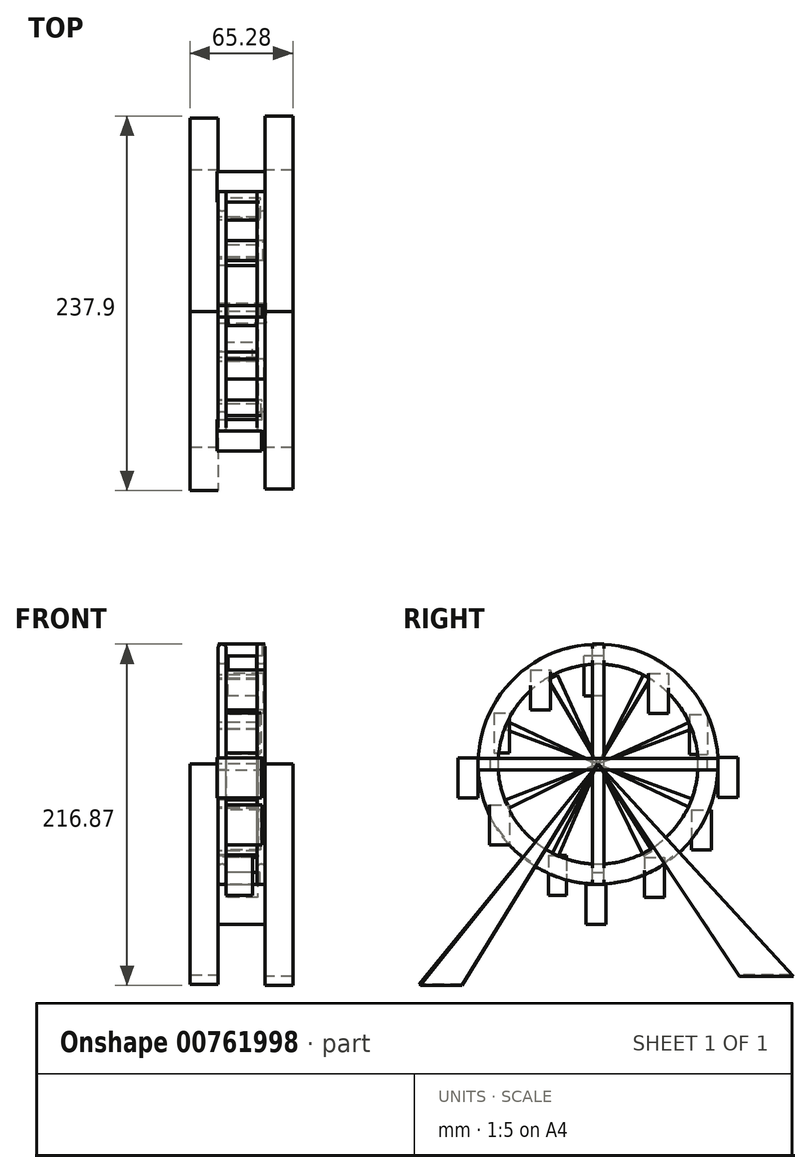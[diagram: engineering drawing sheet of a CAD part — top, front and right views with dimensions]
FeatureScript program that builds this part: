
annotation { "Feature Type Name" : "Feature", "Feature Type Description" : "" }
export const myFeature = defineFeature(function(context is Context, id is Id, definition is map)
    precondition{}
    {
        {
            var Q0;
            Q0=qCreatedBy(makeId("Right.planeOp"),FACE);
            var sketch = newSketch(context, id + "F0", { "sketchPlane" : qUnion([Q0])});
            skCircle(sketch, "E0", {"center": v(0, 0) * mm, "radius": 76.2 * mm});
            skSolve(sketch);
        }
        {
            var Q0;
            Q0 = qSketchRegion(id + "F0", true);
            extrude(context, id + "F1", {"entities" : qUnion([Q0]), "depth" : 5.08 * mm, "offsetDistance" : 25.4 * mm});
        }
        {
            var Q0;
            Q0=makeQuery(id+"F1.opExtrude","CAP_FACE",FACE,{"disambiguationData":[OSD([sQuery(id+"F0.wireOp",EDGE,"E0")])],"isStart":false});
            var sketch = newSketch(context, id + "F2", { "sketchPlane" : qUnion([Q0])});
            skCircle(sketch, "E1", {"center": v(0, 0) * mm, "radius": 63.5 * mm});
            skSolve(sketch);
        }
        {
            var Q0;
            Q0 = qSketchRegion(id + "F2", true);
            extrude(context, id + "F3", {"entities" : qUnion([Q0]), "operationType" : NewBodyOperationType.REMOVE, "endBound" : BoundingType.SYMMETRIC, "oppositeDirection" : true, "depth" : 56.9 * mm, "offsetDistance" : 25.4 * mm});
        }
        {
            var Q0;
            Q0=qCreatedBy(makeId("Right.planeOp"),FACE);
            var sketch = newSketch(context, id + "F4", { "sketchPlane" : qUnion([Q0])});
            skLineSegment(sketch, "E2.bottom", {"start": v(4.1, -63.24) * mm, "end": v(-4.1, -63.24) * mm});
            skLineSegment(sketch, "E2.top", {"start": v(4.1, 63.24) * mm, "end": v(-4.1, 63.24) * mm});
            skLineSegment(sketch, "E2.left", {"start": v(4.1, -63.24) * mm, "end": v(4.1, 63.24) * mm});
            skLineSegment(sketch, "E2.right", {"start": v(-4.1, -63.24) * mm, "end": v(-4.1, 63.24) * mm});
            skPoint(sketch, "E2.middle", {"position": v(0, 0) * mm});
            skSolve(sketch);
        }
        {
            var Q0;
            Q0=makeQuery(id+"F1.opExtrude","SWEPT_BODY",BODY,{"disambiguationData":[OSD([sQuery(id+"F0.wireOp",EDGE,"E0")])]});
            transform(context, id + "F5", {"entities" : qUnion([Q0]), "transformType" : TransformType.TRANSLATION_3D, "dx" : 9.4 * mm, "dy" : 0 * mm, "dz" : 0 * mm, "makeCopy" : true});
        }
        {
            var Q0;
            Q0=makeQuery(id+"F5.opPattern","COPY",BODY,{"derivedFrom":makeQuery(id+"F1.opExtrude","SWEPT_BODY",BODY,{"disambiguationData":[OSD([sQuery(id+"F0.wireOp",EDGE,"E0")])]}),"instanceName":"1"});
            transform(context, id + "F6", {"entities" : qUnion([Q0]), "transformType" : TransformType.TRANSLATION_3D, "dx" : 15.5 * mm, "dy" : 0 * mm, "dz" : 0 * mm, "makeCopy" : true});
        }
        {
            var Q0;
            Q0=makeQuery(id+"F5.opPattern","COPY",BODY,{"derivedFrom":makeQuery(id+"F1.opExtrude","SWEPT_BODY",BODY,{"disambiguationData":[OSD([sQuery(id+"F0.wireOp",EDGE,"E0")])]}),"instanceName":"1"});
            deleteBodies(context, id + "F7", {"entities" : qUnion([Q0])});
        }
        {
            var Q0;
            Q0=makeQuery(id+"F1.opExtrude","CAP_EDGE",EDGE,{"disambiguationData":[OSD([sQuery(id+"F0.wireOp",EDGE,"E0")])],"isStart":true});
            fillet(context, id + "F8", {"entities" : qUnion([Q0]), "radius" : 2.54 * mm, "tangentPropagation" : true, "allowEdgeOverflow" : false});
        }
        {
            var Q0;
            Q0=makeQuery(id+"F1.opExtrude","CAP_EDGE",EDGE,{"disambiguationData":[OSD([sQuery(id+"F0.wireOp",EDGE,"E0")])],"isStart":false});
            fillet(context, id + "F9", {"entities" : qUnion([Q0]), "radius" : 2.54 * mm, "tangentPropagation" : true, "allowEdgeOverflow" : false});
        }
        {
            var Q0;
            Q0=makeQuery(id+"F3.boolean.opBoolean","INTERSECT",EDGE,{"derivedFrom":[makeQuery(id+"F1.opExtrude","CAP_FACE",FACE,{"disambiguationData":[OSD([sQuery(id+"F0.wireOp",EDGE,"E0")])],"isStart":true}),makeQuery(id+"F3.opExtrude","SWEPT_FACE",FACE,{"disambiguationData":[OSD([sQuery(id+"F2.wireOp",EDGE,"E1")])]})]});
            fillet(context, id + "F10", {"entities" : qUnion([Q0]), "radius" : 2.54 * mm, "tangentPropagation" : true, "allowEdgeOverflow" : false});
        }
        {
            var Q0;
            Q0=makeQuery(id+"F3.boolean.opBoolean","INTERSECT",EDGE,{"derivedFrom":[makeQuery(id+"F1.opExtrude","CAP_FACE",FACE,{"disambiguationData":[OSD([sQuery(id+"F0.wireOp",EDGE,"E0")])],"isStart":false}),makeQuery(id+"F3.opExtrude","SWEPT_FACE",FACE,{"disambiguationData":[OSD([sQuery(id+"F2.wireOp",EDGE,"E1")])]})]});
            fillet(context, id + "F11", {"entities" : qUnion([Q0]), "radius" : 2.54 * mm, "tangentPropagation" : true, "allowEdgeOverflow" : false});
        }
        {
            var Q0;
            Q0=makeQuery(id+"F6.opPattern","COPY",EDGE,{"derivedFrom":makeQuery(id+"F5.opPattern","COPY",EDGE,{"derivedFrom":makeQuery(id+"F1.opExtrude","CAP_EDGE",EDGE,{"disambiguationData":[OSD([sQuery(id+"F0.wireOp",EDGE,"E0")])],"isStart":true}),"instanceName":"1"}),"instanceName":"1"});
            var Q1;
            Q1=makeQuery(id+"F6.opPattern","COPY",EDGE,{"derivedFrom":makeQuery(id+"F5.opPattern","COPY",EDGE,{"derivedFrom":makeQuery(id+"F3.boolean.opBoolean","INTERSECT",EDGE,{"derivedFrom":[makeQuery(id+"F1.opExtrude","CAP_FACE",FACE,{"disambiguationData":[OSD([sQuery(id+"F0.wireOp",EDGE,"E0")])],"isStart":true}),makeQuery(id+"F3.opExtrude","SWEPT_FACE",FACE,{"disambiguationData":[OSD([sQuery(id+"F2.wireOp",EDGE,"E1")])]})]}),"instanceName":"1"}),"instanceName":"1"});
            var Q2;
            Q2=makeQuery(id+"F6.opPattern","COPY",EDGE,{"derivedFrom":makeQuery(id+"F5.opPattern","COPY",EDGE,{"derivedFrom":makeQuery(id+"F3.boolean.opBoolean","INTERSECT",EDGE,{"derivedFrom":[makeQuery(id+"F1.opExtrude","CAP_FACE",FACE,{"disambiguationData":[OSD([sQuery(id+"F0.wireOp",EDGE,"E0")])],"isStart":false}),makeQuery(id+"F3.opExtrude","SWEPT_FACE",FACE,{"disambiguationData":[OSD([sQuery(id+"F2.wireOp",EDGE,"E1")])]})]}),"instanceName":"1"}),"instanceName":"1"});
            var Q3;
            Q3=makeQuery(id+"F6.opPattern","COPY",EDGE,{"derivedFrom":makeQuery(id+"F5.opPattern","COPY",EDGE,{"derivedFrom":makeQuery(id+"F1.opExtrude","CAP_EDGE",EDGE,{"disambiguationData":[OSD([sQuery(id+"F0.wireOp",EDGE,"E0")])],"isStart":false}),"instanceName":"1"}),"instanceName":"1"});
            fillet(context, id + "F12", {"entities" : qUnion([Q0, Q1, Q2, Q3]), "radius" : 2.54 * mm, "tangentPropagation" : true, "allowEdgeOverflow" : false});
        }
        {
            var Q0;
            Q0=qCreatedBy(makeId("Right.planeOp"),FACE);
            var sketch = newSketch(context, id + "F13", { "sketchPlane" : qUnion([Q0])});
            skLineSegment(sketch, "E3.bottom", {"start": v(3.62, -76.27) * mm, "end": v(-3.62, -76.27) * mm});
            skLineSegment(sketch, "E3.top", {"start": v(3.62, 76.27) * mm, "end": v(-3.62, 76.27) * mm});
            skLineSegment(sketch, "E3.left", {"start": v(3.62, -76.27) * mm, "end": v(3.62, 76.27) * mm});
            skLineSegment(sketch, "E3.right", {"start": v(-3.62, -76.27) * mm, "end": v(-3.62, 76.27) * mm});
            skPoint(sketch, "E3.middle", {"position": v(0, 0) * mm});
            skSolve(sketch);
        }
        {
            var Q0;
            Q0 = qSketchRegion(id + "F13", true);
            extrude(context, id + "F14", {"entities" : qUnion([Q0]), "depth" : 5.08 * mm, "offsetDistance" : 25.4 * mm});
        }
        {
            var Q0;
            Q0=makeQuery(id+"F14.opExtrude","SWEPT_BODY",BODY,{"disambiguationData":[OSD([sQuery(id+"F13.wireOp",EDGE,"E3.bottom"),sQuery(id+"F13.wireOp",EDGE,"E3.top"),sQuery(id+"F13.wireOp",EDGE,"E3.left"),sQuery(id+"F13.wireOp",EDGE,"E3.right")])]});
            transform(context, id + "F15", {"entities" : qUnion([Q0]), "transformType" : TransformType.TRANSLATION_3D, "dx" : 17.02 * mm, "dy" : 0 * mm, "dz" : 0 * mm, "makeCopy" : true});
        }
        {
            var Q0;
            Q0=makeQuery(id+"F15.opPattern","COPY",BODY,{"derivedFrom":makeQuery(id+"F14.opExtrude","SWEPT_BODY",BODY,{"disambiguationData":[OSD([sQuery(id+"F13.wireOp",EDGE,"E3.bottom"),sQuery(id+"F13.wireOp",EDGE,"E3.top"),sQuery(id+"F13.wireOp",EDGE,"E3.left"),sQuery(id+"F13.wireOp",EDGE,"E3.right")])]}),"instanceName":"1"});
            transform(context, id + "F16", {"entities" : qUnion([Q0]), "transformType" : TransformType.TRANSLATION_3D, "dx" : 7.62 * mm, "dy" : 0 * mm, "dz" : 0 * mm, "makeCopy" : true});
        }
        {
            var Q0;
            Q0=makeQuery(id+"F15.opPattern","COPY",BODY,{"derivedFrom":makeQuery(id+"F14.opExtrude","SWEPT_BODY",BODY,{"disambiguationData":[OSD([sQuery(id+"F13.wireOp",EDGE,"E3.bottom"),sQuery(id+"F13.wireOp",EDGE,"E3.top"),sQuery(id+"F13.wireOp",EDGE,"E3.left"),sQuery(id+"F13.wireOp",EDGE,"E3.right")])]}),"instanceName":"1"});
            deleteBodies(context, id + "F17", {"entities" : qUnion([Q0])});
        }
        {
            var Q0;
            Q0=makeQuery(id+"F14.opExtrude","CAP_FACE",FACE,{"disambiguationData":[OSD([sQuery(id+"F13.wireOp",EDGE,"E3.bottom"),sQuery(id+"F13.wireOp",EDGE,"E3.top"),sQuery(id+"F13.wireOp",EDGE,"E3.left"),sQuery(id+"F13.wireOp",EDGE,"E3.right")])],"isStart":false});
            var sketch = newSketch(context, id + "F18", { "sketchPlane" : qUnion([Q0])});
            skLineSegment(sketch, "E4.bottom", {"start": v(-3.62, 76.27) * mm, "end": v(3.62, 76.27) * mm});
            skLineSegment(sketch, "E4.top", {"start": v(-3.62, 68.65) * mm, "end": v(3.62, 68.65) * mm});
            skLineSegment(sketch, "E4.left", {"start": v(-3.62, 76.27) * mm, "end": v(-3.62, 68.65) * mm});
            skLineSegment(sketch, "E4.right", {"start": v(3.62, 76.27) * mm, "end": v(3.62, 68.65) * mm});
            skSolve(sketch);
        }
        {
            var Q0;
            Q0 = qSketchRegion(id + "F18", true);
            extrude(context, id + "F19", {"entities" : qUnion([Q0]), "depth" : 23.1 * mm, "offsetDistance" : 25.4 * mm});
        }
        {
            var Q0;
            Q0=makeQuery(id+"F14.opExtrude","CAP_FACE",FACE,{"disambiguationData":[OSD([sQuery(id+"F13.wireOp",EDGE,"E3.bottom"),sQuery(id+"F13.wireOp",EDGE,"E3.top"),sQuery(id+"F13.wireOp",EDGE,"E3.left"),sQuery(id+"F13.wireOp",EDGE,"E3.right")])],"isStart":false});
            var sketch = newSketch(context, id + "F20", { "sketchPlane" : qUnion([Q0])});
            skLineSegment(sketch, "E5.bottom", {"start": v(-3.62, -76.27) * mm, "end": v(3.62, -76.27) * mm});
            skLineSegment(sketch, "E5.top", {"start": v(-3.62, -68.65) * mm, "end": v(3.62, -68.65) * mm});
            skLineSegment(sketch, "E5.left", {"start": v(-3.62, -76.27) * mm, "end": v(-3.62, -68.65) * mm});
            skLineSegment(sketch, "E5.right", {"start": v(3.62, -76.27) * mm, "end": v(3.62, -68.65) * mm});
            skSolve(sketch);
        }
        {
            var Q0;
            Q0 = qSketchRegion(id + "F20", true);
            extrude(context, id + "F21", {"entities" : qUnion([Q0]), "depth" : 21.59 * mm, "offsetDistance" : 25.4 * mm});
        }
        {
            var Q0;
            Q0=qCreatedBy(makeId("Right.planeOp"),FACE);
            var sketch = newSketch(context, id + "F22", { "sketchPlane" : qUnion([Q0])});
            skLineSegment(sketch, "E6.bottom", {"start": v(76.2, -3.62) * mm, "end": v(-76.2, -3.62) * mm});
            skLineSegment(sketch, "E6.top", {"start": v(76.2, 3.62) * mm, "end": v(-76.2, 3.62) * mm});
            skLineSegment(sketch, "E6.left", {"start": v(76.2, -3.62) * mm, "end": v(76.2, 3.62) * mm});
            skLineSegment(sketch, "E6.right", {"start": v(-76.2, -3.62) * mm, "end": v(-76.2, 3.62) * mm});
            skPoint(sketch, "E6.middle", {"position": v(0, 0) * mm});
            skSolve(sketch);
        }
        {
            var Q0;
            Q0=makeQuery(id+"F22.imprint","IMPRINT",FACE,{"disambiguationData":[TD([[makeQuery(id+"F22.imprint","IMPRINT",EDGE,{"derivedFrom":sQuery(id+"F22.wireOp",EDGE,"E6.bottom")}),-1.0]])]});
            extrude(context, id + "F23", {"entities" : qUnion([Q0]), "depth" : 5.08 * mm, "offsetDistance" : 25.4 * mm});
        }
        {
            var Q0;
            Q0=makeQuery(id+"F23.opExtrude","SWEPT_BODY",BODY,{"disambiguationData":[OSD([sQuery(id+"F22.wireOp",EDGE,"E6.bottom"),sQuery(id+"F22.wireOp",EDGE,"E6.top"),sQuery(id+"F22.wireOp",EDGE,"E6.left"),sQuery(id+"F22.wireOp",EDGE,"E6.right")])]});
            transform(context, id + "F24", {"entities" : qUnion([Q0]), "transformType" : TransformType.TRANSLATION_3D, "dx" : 24.9 * mm, "dy" : 0 * mm, "dz" : 0 * mm, "makeCopy" : true});
        }
        {
            var Q0;
            Q0=makeQuery(id+"F6.opPattern","COPY",FACE,{"derivedFrom":makeQuery(id+"F5.opPattern","COPY",FACE,{"derivedFrom":makeQuery(id+"F1.opExtrude","CAP_FACE",FACE,{"disambiguationData":[OSD([sQuery(id+"F0.wireOp",EDGE,"E0")])],"isStart":true}),"instanceName":"1"}),"instanceName":"1"});
            var sketch = newSketch(context, id + "F25", { "sketchPlane" : qUnion([Q0])});
            skLineSegment(sketch, "E7.bottom", {"start": v(76.13, 3.8) * mm, "end": v(68.62, 3.8) * mm});
            skLineSegment(sketch, "E7.top", {"start": v(76.13, -3.79) * mm, "end": v(68.62, -3.79) * mm});
            skLineSegment(sketch, "E7.left", {"start": v(76.13, 3.8) * mm, "end": v(76.13, -3.79) * mm});
            skLineSegment(sketch, "E7.right", {"start": v(68.62, 3.8) * mm, "end": v(68.62, -3.79) * mm});
            skSolve(sketch);
        }
        {
            var Q0;
            Q0 = qSketchRegion(id + "F25", true);
            extrude(context, id + "F26", {"entities" : qUnion([Q0]), "depth" : 25.4 * mm, "offsetDistance" : 25.4 * mm});
        }
        {
            var Q0;
            Q0=makeQuery(id+"F6.opPattern","COPY",FACE,{"derivedFrom":makeQuery(id+"F5.opPattern","COPY",FACE,{"derivedFrom":makeQuery(id+"F1.opExtrude","CAP_FACE",FACE,{"disambiguationData":[OSD([sQuery(id+"F0.wireOp",EDGE,"E0")])],"isStart":true}),"instanceName":"1"}),"instanceName":"1"});
            var sketch = newSketch(context, id + "F27", { "sketchPlane" : qUnion([Q0])});
            skLineSegment(sketch, "E8.bottom", {"start": v(-76.07, -3.62) * mm, "end": v(-69.42, -3.62) * mm});
            skLineSegment(sketch, "E8.top", {"start": v(-76.07, 3.53) * mm, "end": v(-69.42, 3.53) * mm});
            skLineSegment(sketch, "E8.left", {"start": v(-76.07, -3.62) * mm, "end": v(-76.07, 3.53) * mm});
            skLineSegment(sketch, "E8.right", {"start": v(-69.42, -3.62) * mm, "end": v(-69.42, 3.53) * mm});
            skSolve(sketch);
        }
        {
            var Q0;
            Q0 = qSketchRegion(id + "F27", true);
            extrude(context, id + "F28", {"entities" : qUnion([Q0]), "depth" : 25.4 * mm, "offsetDistance" : 25.4 * mm});
        }
        {
            var Q0;
            Q0=makeQuery(id+"F26.opExtrude","SWEPT_FACE",FACE,{"disambiguationData":[OSD([sQuery(id+"F25.wireOp",EDGE,"E7.left")])]});
            var sketch = newSketch(context, id + "F29", { "sketchPlane" : qUnion([Q0])});
            skLineSegment(sketch, "E9.bottom", {"start": v(-0.5, 3.8) * mm, "end": v(27.75, 3.8) * mm});
            skLineSegment(sketch, "E9.top", {"start": v(-0.5, -21.6) * mm, "end": v(27.75, -21.6) * mm});
            skLineSegment(sketch, "E9.left", {"start": v(-0.5, 3.8) * mm, "end": v(-0.5, -21.6) * mm});
            skLineSegment(sketch, "E9.right", {"start": v(27.75, 3.8) * mm, "end": v(27.75, -21.6) * mm});
            skSolve(sketch);
        }
        {
            var Q0;
            Q0 = qSketchRegion(id + "F29", true);
            extrude(context, id + "F30", {"entities" : qUnion([Q0]), "depth" : 12.7 * mm, "offsetDistance" : 25.4 * mm});
        }
        {
            var Q0;
            Q0=makeQuery(id+"F28.opExtrude","SWEPT_FACE",FACE,{"disambiguationData":[OSD([sQuery(id+"F27.wireOp",EDGE,"E8.left")])]});
            var sketch = newSketch(context, id + "F31", { "sketchPlane" : qUnion([Q0])});
            skLineSegment(sketch, "E10.bottom", {"start": v(-29.97, 4.2) * mm, "end": v(0.5, 4.2) * mm});
            skLineSegment(sketch, "E10.top", {"start": v(-29.97, -21.2) * mm, "end": v(0.5, -21.2) * mm});
            skLineSegment(sketch, "E10.left", {"start": v(-29.97, 4.2) * mm, "end": v(-29.97, -21.2) * mm});
            skLineSegment(sketch, "E10.right", {"start": v(0.5, 4.2) * mm, "end": v(0.5, -21.2) * mm});
            skSolve(sketch);
        }
        {
            var Q0;
            Q0 = qSketchRegion(id + "F31", true);
            extrude(context, id + "F32", {"entities" : qUnion([Q0]), "depth" : 12.7 * mm, "offsetDistance" : 25.4 * mm});
        }
        {
            var Q0;
            Q0=makeQuery(id+"F21.opExtrude","SWEPT_FACE",FACE,{"disambiguationData":[OSD([sQuery(id+"F20.wireOp",EDGE,"E5.bottom")])]});
            var sketch = newSketch(context, id + "F33", { "sketchPlane" : qUnion([Q0])});
            skLineSegment(sketch, "E11.bottom", {"start": v(0, -5.15) * mm, "end": v(30.32, -5.15) * mm});
            skLineSegment(sketch, "E11.top", {"start": v(0, 7.55) * mm, "end": v(30.32, 7.55) * mm});
            skLineSegment(sketch, "E11.left", {"start": v(0, -5.15) * mm, "end": v(0, 7.55) * mm});
            skLineSegment(sketch, "E11.right", {"start": v(30.32, -5.15) * mm, "end": v(30.32, 7.55) * mm});
            skSolve(sketch);
        }
        {
            var Q0;
            Q0 = qSketchRegion(id + "F33", true);
            extrude(context, id + "F34", {"entities" : qUnion([Q0]), "depth" : 25.4 * mm, "offsetDistance" : 25.4 * mm});
        }
        {
            var Q0;
            Q0=makeQuery(id+"F19.opExtrude","SWEPT_FACE",FACE,{"disambiguationData":[OSD([sQuery(id+"F18.wireOp",EDGE,"E4.top")])]});
            var sketch = newSketch(context, id + "F35", { "sketchPlane" : qUnion([Q0])});
            skLineSegment(sketch, "E12.bottom", {"start": v(24.52, -3.62) * mm, "end": v(6.24, -3.62) * mm});
            skLineSegment(sketch, "E12.top", {"start": v(24.52, 9.08) * mm, "end": v(6.24, 9.08) * mm});
            skLineSegment(sketch, "E12.left", {"start": v(24.52, -3.62) * mm, "end": v(24.52, 9.08) * mm});
            skLineSegment(sketch, "E12.right", {"start": v(6.24, -3.62) * mm, "end": v(6.24, 9.08) * mm});
            skSolve(sketch);
        }
        {
            var Q0;
            Q0 = qSketchRegion(id + "F35", true);
            extrude(context, id + "F36", {"entities" : qUnion([Q0]), "operationType" : NewBodyOperationType.ADD, "depth" : 25.4 * mm, "offsetDistance" : 25.4 * mm});
        }
        {
            var Q0;
            Q0=makeQuery(id+"F16.opPattern","COPY",FACE,{"derivedFrom":makeQuery(id+"F15.opPattern","COPY",FACE,{"derivedFrom":makeQuery(id+"F14.opExtrude","CAP_FACE",FACE,{"disambiguationData":[OSD([sQuery(id+"F13.wireOp",EDGE,"E3.bottom"),sQuery(id+"F13.wireOp",EDGE,"E3.top"),sQuery(id+"F13.wireOp",EDGE,"E3.left"),sQuery(id+"F13.wireOp",EDGE,"E3.right")])],"isStart":false}),"instanceName":"1"}),"instanceName":"1"});
            var sketch = newSketch(context, id + "F37", { "sketchPlane" : qUnion([Q0])});
            skLineSegment(sketch, "E13", {"start": v(0, 0) * mm, "end": v(-112.83, -140.6) * mm});
            skLineSegment(sketch, "E14", {"start": v(-112.83, -140.6) * mm, "end": v(-86.48, -140.6) * mm});
            skLineSegment(sketch, "E15", {"start": v(-86.48, -140.6) * mm, "end": v(0, 0) * mm});
            skLineSegment(sketch, "E16", {"start": v(0, 0) * mm, "end": v(124.05, -134.9) * mm});
            skLineSegment(sketch, "E17", {"start": v(124.05, -134.9) * mm, "end": v(89.82, -134.9) * mm});
            skLineSegment(sketch, "E18", {"start": v(89.82, -134.9) * mm, "end": v(0, 0) * mm});
            skSolve(sketch);
        }
        {
            var Q0;
            Q0 = qSketchRegion(id + "F37", true);
            extrude(context, id + "F38", {"entities" : qUnion([Q0]), "depth" : 17.78 * mm, "offsetDistance" : 25.4 * mm});
        }
        {
            var Q0;
            Q0=makeQuery(id+"F4.imprint","IMPRINT",FACE,{"disambiguationData":[TD([[makeQuery(id+"F4.imprint","IMPRINT",EDGE,{"derivedFrom":sQuery(id+"F4.wireOp",EDGE,"E2.bottom")}),-1.0]])]});
            var sketch = newSketch(context, id + "F39", { "sketchPlane" : qUnion([Q0])});
            skLineSegment(sketch, "E19", {"start": v(0, 0) * mm, "end": v(122.75, -133.76) * mm});
            skLineSegment(sketch, "E20", {"start": v(122.75, -133.76) * mm, "end": v(89.96, -133.76) * mm});
            skLineSegment(sketch, "E21", {"start": v(89.96, -133.76) * mm, "end": v(0, 0) * mm});
            skLineSegment(sketch, "E22", {"start": v(0, 0) * mm, "end": v(-86.2, -139.85) * mm});
            skLineSegment(sketch, "E23", {"start": v(-86.2, -139.85) * mm, "end": v(-113.85, -139.85) * mm});
            skLineSegment(sketch, "E24", {"start": v(-113.85, -139.85) * mm, "end": v(0, 0) * mm});
            skSolve(sketch);
        }
        {
            var Q0;
            Q0 = qSketchRegion(id + "F39", true);
            extrude(context, id + "F40", {"entities" : qUnion([Q0]), "oppositeDirection" : true, "depth" : 17.78 * mm, "offsetDistance" : 25.4 * mm});
        }
        {
            var Q0;
            Q0=qCreatedBy(makeId("Right.planeOp"),FACE);
            var sketch = newSketch(context, id + "F41", { "sketchPlane" : qUnion([Q0])});
            skLineSegment(sketch, "E25", {"start": v(0, 0) * mm, "end": v(28.94, 56.61) * mm});
            skLineSegment(sketch, "E26", {"start": v(28.94, 56.61) * mm, "end": v(33.17, 54.45) * mm});
            skLineSegment(sketch, "E27", {"start": v(33.17, 54.45) * mm, "end": v(0, 0) * mm});
            skLineSegment(sketch, "E28", {"start": v(0, 0) * mm, "end": v(58.07, 26.54) * mm});
            skLineSegment(sketch, "E29", {"start": v(58.07, 26.54) * mm, "end": v(59.97, 22.37) * mm});
            skLineSegment(sketch, "E30", {"start": v(59.97, 22.37) * mm, "end": v(0, 0) * mm});
            skLineSegment(sketch, "E31", {"start": v(0, 0) * mm, "end": v(-25.88, 56.61) * mm});
            skLineSegment(sketch, "E32", {"start": v(-25.88, 56.61) * mm, "end": v(-31.9, 53.86) * mm});
            skLineSegment(sketch, "E33", {"start": v(-31.9, 53.86) * mm, "end": v(0, 0) * mm});
            skLineSegment(sketch, "E34", {"start": v(0, 0) * mm, "end": v(-56.75, 26.54) * mm});
            skLineSegment(sketch, "E35", {"start": v(-56.75, 26.54) * mm, "end": v(-58.92, 21.9) * mm});
            skLineSegment(sketch, "E36", {"start": v(-58.92, 21.9) * mm, "end": v(0, 0) * mm});
            skLineSegment(sketch, "E37", {"start": v(0, 0) * mm, "end": v(-58.92, -22.6) * mm});
            skLineSegment(sketch, "E38", {"start": v(-58.92, -22.6) * mm, "end": v(-56.44, -28.01) * mm});
            skLineSegment(sketch, "E39", {"start": v(-56.44, -28.01) * mm, "end": v(0, 0) * mm});
            skLineSegment(sketch, "E40", {"start": v(0, 0) * mm, "end": v(-29.46, -57.62) * mm});
            skPoint(sketch, "E40.endSnap0", {"position": v(-29.46, -11.3) * mm});
            skLineSegment(sketch, "E41", {"start": v(-29.46, -57.62) * mm, "end": v(-25.58, -59.06) * mm});
            skLineSegment(sketch, "E42", {"start": v(-25.58, -59.06) * mm, "end": v(0, 0) * mm});
            skLineSegment(sketch, "E43", {"start": v(0, 0) * mm, "end": v(28.94, -58.31) * mm});
            skLineSegment(sketch, "E44", {"start": v(28.94, -58.31) * mm, "end": v(34.37, -55.1) * mm});
            skLineSegment(sketch, "E45", {"start": v(34.37, -55.1) * mm, "end": v(0, 0) * mm});
            skLineSegment(sketch, "E46", {"start": v(0, 0) * mm, "end": v(59.97, -22.3) * mm});
            skLineSegment(sketch, "E47", {"start": v(59.97, -22.3) * mm, "end": v(58.07, -27.42) * mm});
            skLineSegment(sketch, "E48", {"start": v(58.07, -27.42) * mm, "end": v(0, 0) * mm});
            skSolve(sketch);
        }
        {
            var Q0;
            Q0 = qSketchRegion(id + "F41", true);
            extrude(context, id + "F42", {"entities" : qUnion([Q0]), "depth" : 25.4 * mm, "offsetDistance" : 25.4 * mm});
        }
        {
            var Q0;
            Q0=makeQuery(id+"F1.opExtrude","CAP_FACE",FACE,{"disambiguationData":[OSD([sQuery(id+"F0.wireOp",EDGE,"E0")])],"isStart":false});
            var sketch = newSketch(context, id + "F43", { "sketchPlane" : qUnion([Q0])});
            skLineSegment(sketch, "E49.bottom", {"start": v(-43.07, 59.76) * mm, "end": v(-30.37, 59.76) * mm});
            skLineSegment(sketch, "E49.top", {"start": v(-43.07, 34.36) * mm, "end": v(-30.37, 34.36) * mm});
            skLineSegment(sketch, "E49.left", {"start": v(-43.07, 59.76) * mm, "end": v(-43.07, 34.36) * mm});
            skLineSegment(sketch, "E49.right", {"start": v(-30.37, 59.76) * mm, "end": v(-30.37, 34.36) * mm});
            skSolve(sketch);
        }
        {
            var Q0;
            Q0 = qSketchRegion(id + "F43", true);
            extrude(context, id + "F44", {"entities" : qUnion([Q0]), "depth" : 24.13 * mm, "offsetDistance" : 25.4 * mm});
        }
        {
            var Q0;
            Q0=makeQuery(id+"F1.opExtrude","CAP_FACE",FACE,{"disambiguationData":[OSD([sQuery(id+"F0.wireOp",EDGE,"E0")])],"isStart":false});
            var sketch = newSketch(context, id + "F45", { "sketchPlane" : qUnion([Q0])});
            skLineSegment(sketch, "E50.bottom", {"start": v(-66.16, 32.38) * mm, "end": v(-56.37, 32.38) * mm});
            skLineSegment(sketch, "E50.top", {"start": v(-66.16, 6.98) * mm, "end": v(-56.37, 6.98) * mm});
            skLineSegment(sketch, "E50.left", {"start": v(-66.16, 32.38) * mm, "end": v(-66.16, 6.98) * mm});
            skLineSegment(sketch, "E50.right", {"start": v(-56.37, 32.38) * mm, "end": v(-56.37, 6.98) * mm});
            skSolve(sketch);
        }
        {
            var Q0;
            Q0 = qSketchRegion(id + "F45", true);
            extrude(context, id + "F46", {"entities" : qUnion([Q0]), "depth" : 22.35 * mm, "offsetDistance" : 25.4 * mm});
        }
        {
            var Q0;
            Q0=makeQuery(id+"F1.opExtrude","CAP_FACE",FACE,{"disambiguationData":[OSD([sQuery(id+"F0.wireOp",EDGE,"E0")])],"isStart":false});
            var sketch = newSketch(context, id + "F47", { "sketchPlane" : qUnion([Q0])});
            skLineSegment(sketch, "E51.bottom", {"start": v(-68.93, -25.97) * mm, "end": v(-56.23, -25.97) * mm});
            skLineSegment(sketch, "E51.top", {"start": v(-68.93, -51.37) * mm, "end": v(-56.23, -51.37) * mm});
            skLineSegment(sketch, "E51.left", {"start": v(-68.93, -25.97) * mm, "end": v(-68.93, -51.37) * mm});
            skLineSegment(sketch, "E51.right", {"start": v(-56.23, -25.97) * mm, "end": v(-56.23, -51.37) * mm});
            skSolve(sketch);
        }
        {
            var Q0;
            Q0 = qSketchRegion(id + "F47", true);
            extrude(context, id + "F48", {"entities" : qUnion([Q0]), "depth" : 22.86 * mm, "offsetDistance" : 25.4 * mm});
        }
        {
            var Q0;
            Q0=makeQuery(id+"F1.opExtrude","CAP_FACE",FACE,{"disambiguationData":[OSD([sQuery(id+"F0.wireOp",EDGE,"E0")])],"isStart":false});
            var sketch = newSketch(context, id + "F49", { "sketchPlane" : qUnion([Q0])});
            skLineSegment(sketch, "E52.bottom", {"start": v(-31.46, -58.07) * mm, "end": v(-19.97, -58.07) * mm});
            skLineSegment(sketch, "E52.top", {"start": v(-31.46, -83.47) * mm, "end": v(-19.97, -83.47) * mm});
            skLineSegment(sketch, "E52.left", {"start": v(-31.46, -58.07) * mm, "end": v(-31.46, -83.47) * mm});
            skLineSegment(sketch, "E52.right", {"start": v(-19.97, -58.07) * mm, "end": v(-19.97, -83.47) * mm});
            skSolve(sketch);
        }
        {
            var Q0;
            Q0 = qSketchRegion(id + "F49", true);
            extrude(context, id + "F50", {"entities" : qUnion([Q0]), "depth" : 16.76 * mm, "offsetDistance" : 25.4 * mm});
        }
        {
            var Q0;
            Q0=makeQuery(id+"F1.opExtrude","CAP_FACE",FACE,{"disambiguationData":[OSD([sQuery(id+"F0.wireOp",EDGE,"E0")])],"isStart":false});
            var sketch = newSketch(context, id + "F51", { "sketchPlane" : qUnion([Q0])});
            skLineSegment(sketch, "E53.bottom", {"start": v(29.4, -59.13) * mm, "end": v(42.1, -59.13) * mm});
            skLineSegment(sketch, "E53.top", {"start": v(29.4, -84.53) * mm, "end": v(42.1, -84.53) * mm});
            skLineSegment(sketch, "E53.left", {"start": v(29.4, -59.13) * mm, "end": v(29.4, -84.53) * mm});
            skLineSegment(sketch, "E53.right", {"start": v(42.1, -59.13) * mm, "end": v(42.1, -84.53) * mm});
            skSolve(sketch);
        }
        {
            var Q0;
            Q0 = qSketchRegion(id + "F51", true);
            extrude(context, id + "F52", {"entities" : qUnion([Q0]), "depth" : 20.07 * mm, "offsetDistance" : 25.4 * mm});
        }
        {
            var Q0;
            Q0=makeQuery(id+"F1.opExtrude","CAP_FACE",FACE,{"disambiguationData":[OSD([sQuery(id+"F0.wireOp",EDGE,"E0")])],"isStart":false});
            var sketch = newSketch(context, id + "F53", { "sketchPlane" : qUnion([Q0])});
            skLineSegment(sketch, "E54.bottom", {"start": v(59.27, -29.12) * mm, "end": v(71.97, -29.12) * mm});
            skLineSegment(sketch, "E54.top", {"start": v(59.27, -54.52) * mm, "end": v(71.97, -54.52) * mm});
            skLineSegment(sketch, "E54.left", {"start": v(59.27, -29.12) * mm, "end": v(59.27, -54.52) * mm});
            skLineSegment(sketch, "E54.right", {"start": v(71.97, -29.12) * mm, "end": v(71.97, -54.52) * mm});
            skSolve(sketch);
        }
        {
            var Q0;
            Q0 = qSketchRegion(id + "F53", true);
            extrude(context, id + "F54", {"entities" : qUnion([Q0]), "depth" : 21.97 * mm, "offsetDistance" : 25.4 * mm});
        }
        {
            var Q0;
            Q0=makeQuery(id+"F1.opExtrude","CAP_FACE",FACE,{"disambiguationData":[OSD([sQuery(id+"F0.wireOp",EDGE,"E0")])],"isStart":false});
            var sketch = newSketch(context, id + "F55", { "sketchPlane" : qUnion([Q0])});
            skLineSegment(sketch, "E55.bottom", {"start": v(32.08, 57.73) * mm, "end": v(44.78, 57.73) * mm});
            skLineSegment(sketch, "E55.top", {"start": v(32.08, 32.33) * mm, "end": v(44.78, 32.33) * mm});
            skLineSegment(sketch, "E55.left", {"start": v(32.08, 57.73) * mm, "end": v(32.08, 32.33) * mm});
            skLineSegment(sketch, "E55.right", {"start": v(44.78, 57.73) * mm, "end": v(44.78, 32.33) * mm});
            skSolve(sketch);
        }
        {
            var Q0;
            Q0 = qSketchRegion(id + "F55", true);
            extrude(context, id + "F56", {"entities" : qUnion([Q0]), "depth" : 23.62 * mm, "offsetDistance" : 25.4 * mm});
        }
        {
            var Q0;
            Q0=makeQuery(id+"F1.opExtrude","CAP_FACE",FACE,{"disambiguationData":[OSD([sQuery(id+"F0.wireOp",EDGE,"E0")])],"isStart":false});
            var sketch = newSketch(context, id + "F57", { "sketchPlane" : qUnion([Q0])});
            skLineSegment(sketch, "E56.bottom", {"start": v(58, 31.58) * mm, "end": v(69.43, 31.58) * mm});
            skLineSegment(sketch, "E56.top", {"start": v(58, 6.18) * mm, "end": v(69.43, 6.18) * mm});
            skLineSegment(sketch, "E56.left", {"start": v(58, 31.58) * mm, "end": v(58, 6.18) * mm});
            skLineSegment(sketch, "E56.right", {"start": v(69.43, 31.58) * mm, "end": v(69.43, 6.18) * mm});
            skSolve(sketch);
        }
        {
            var Q0;
            Q0 = qSketchRegion(id + "F57", true);
            extrude(context, id + "F58", {"entities" : qUnion([Q0]), "depth" : 21.34 * mm, "offsetDistance" : 25.4 * mm});
        }
    });
